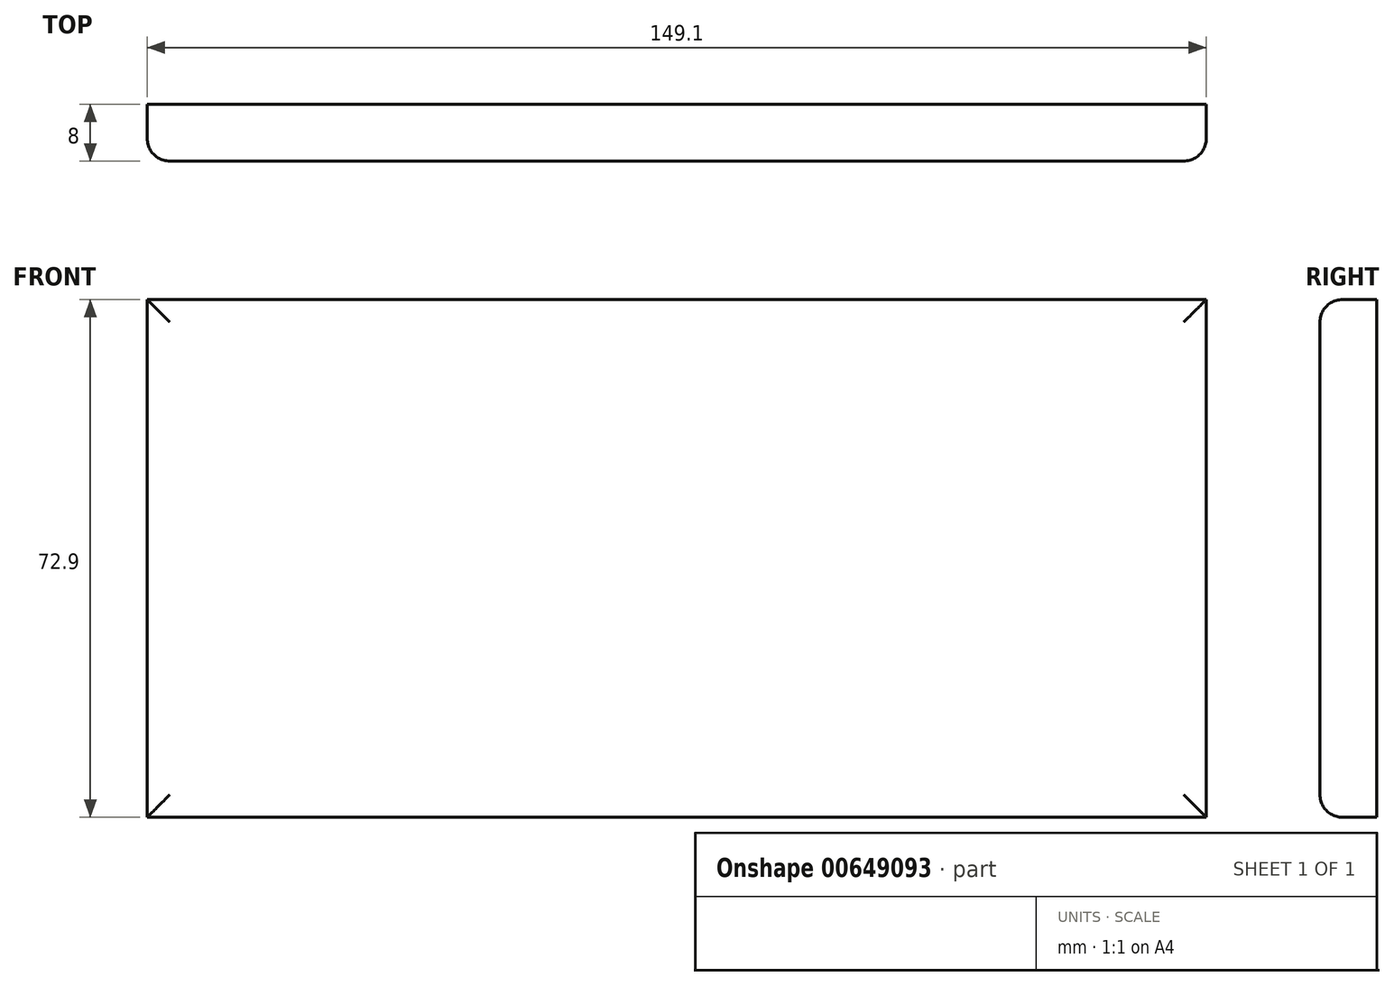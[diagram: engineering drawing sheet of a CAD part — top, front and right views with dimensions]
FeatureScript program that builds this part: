
annotation { "Feature Type Name" : "Feature", "Feature Type Description" : "" }
export const myFeature = defineFeature(function(context is Context, id is Id, definition is map)
    precondition{}
    {
        {
            var Q0;
            Q0=qCreatedBy(makeId("Front.planeOp"),FACE);
            var sketch = newSketch(context, id + "F0", { "sketchPlane" : qUnion([Q0])});
            skLineSegment(sketch, "E0.bottom", {"start": v(74.55, 36.45) * mm, "end": v(-74.55, 36.45) * mm});
            skLineSegment(sketch, "E0.top", {"start": v(74.55, -36.45) * mm, "end": v(-74.55, -36.45) * mm});
            skLineSegment(sketch, "E0.left", {"start": v(74.55, 36.45) * mm, "end": v(74.55, -36.45) * mm});
            skLineSegment(sketch, "E0.right", {"start": v(-74.55, 36.45) * mm, "end": v(-74.55, -36.45) * mm});
            skPoint(sketch, "E0.middle", {"position": v(0, 0) * mm});
            skSolve(sketch);
        }
        {
            var Q0;
            Q0=makeQuery(id+"F0.imprint","IMPRINT",FACE,{"disambiguationData":[TD([[makeQuery(id+"F0.imprint","IMPRINT",EDGE,{"derivedFrom":sQuery(id+"F0.wireOp",EDGE,"E0.bottom")}),1.0]])]});
            extrude(context, id + "F1", {"entities" : qUnion([Q0]), "depth" : 8 * mm, "offsetDistance" : 25.4 * mm});
        }
        {
            var Q0;
            Q0=makeQuery(id+"F1.opExtrude","CAP_EDGE",EDGE,{"disambiguationData":[OSD([sQuery(id+"F0.wireOp",EDGE,"E0.bottom")])],"isStart":false});
            var Q1;
            Q1=makeQuery(id+"F1.opExtrude","CAP_EDGE",EDGE,{"disambiguationData":[OSD([sQuery(id+"F0.wireOp",EDGE,"E0.left")])],"isStart":false});
            var Q2;
            Q2=makeQuery(id+"F1.opExtrude","CAP_EDGE",EDGE,{"disambiguationData":[OSD([sQuery(id+"F0.wireOp",EDGE,"E0.top")])],"isStart":false});
            var Q3;
            Q3=makeQuery(id+"F1.opExtrude","CAP_EDGE",EDGE,{"disambiguationData":[OSD([sQuery(id+"F0.wireOp",EDGE,"E0.right")])],"isStart":false});
            fillet(context, id + "F2", {"entities" : qUnion([Q0, Q1, Q2, Q3]), "radius" : 3.17 * mm, "tangentPropagation" : true, "allowEdgeOverflow" : false});
        }
    });
